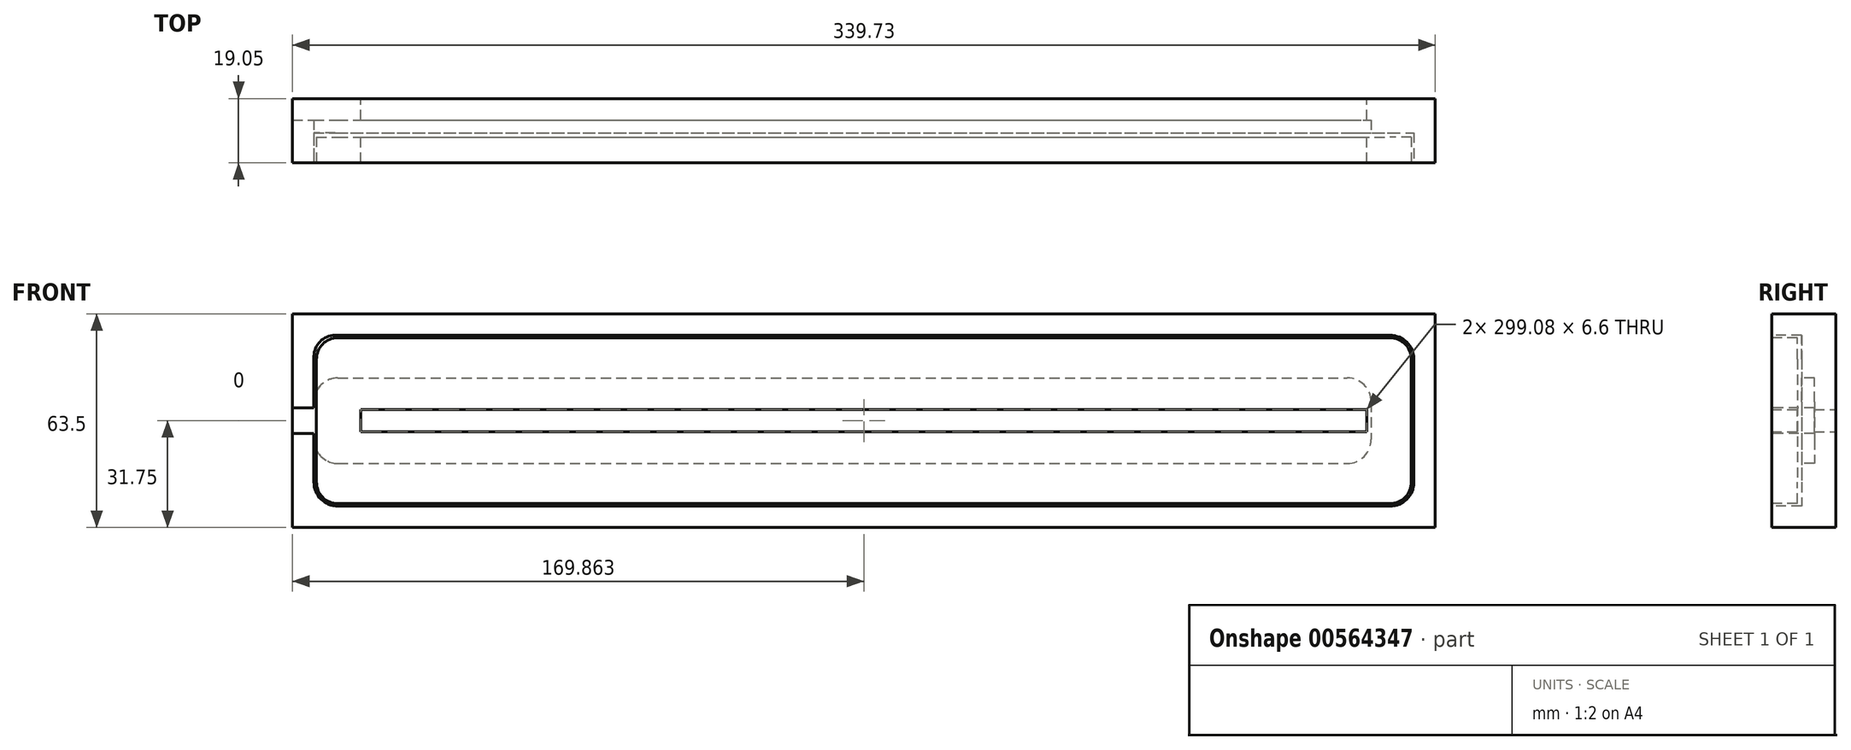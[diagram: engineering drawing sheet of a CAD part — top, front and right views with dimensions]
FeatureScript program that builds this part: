
annotation { "Feature Type Name" : "Feature", "Feature Type Description" : "" }
export const myFeature = defineFeature(function(context is Context, id is Id, definition is map)
    precondition{}
    {
        {
            var Q0;
            Q0=qCreatedBy(makeId("Front.planeOp"),FACE);
            var sketch = newSketch(context, id + "F0", { "sketchPlane" : qUnion([Q0])});
            skLineSegment(sketch, "E0.bottom", {"start": v(0, 0) * mm, "end": v(339.72, 0) * mm});
            skLineSegment(sketch, "E0.top", {"start": v(0, 63.5) * mm, "end": v(339.73, 63.5) * mm});
            skLineSegment(sketch, "E0.left", {"start": v(0, 0) * mm, "end": v(0, 63.5) * mm});
            skLineSegment(sketch, "E0.right", {"start": v(339.73, 0) * mm, "end": v(339.73, 63.5) * mm});
            skSolve(sketch);
        }
        {
            var Q0;
            Q0=makeQuery(id+"F0.imprint","IMPRINT",FACE,{"disambiguationData":[TD([[makeQuery(id+"F0.imprint","IMPRINT",EDGE,{"derivedFrom":sQuery(id+"F0.wireOp",EDGE,"E0.bottom")}),1.0]])]});
            extrude(context, id + "F1", {"entities" : qUnion([Q0]), "depth" : 19.05 * mm, "offsetDistance" : 25.4 * mm});
        }
        {
            var Q0;
            Q0=makeQuery(id+"F1.opExtrude","CAP_FACE",FACE,{"disambiguationData":[OSD([sQuery(id+"F0.wireOp",EDGE,"E0.bottom"),sQuery(id+"F0.wireOp",EDGE,"E0.top"),sQuery(id+"F0.wireOp",EDGE,"E0.left"),sQuery(id+"F0.wireOp",EDGE,"E0.right")])],"isStart":false});
            var sketch = newSketch(context, id + "F2", { "sketchPlane" : qUnion([Q0])});
            skLineSegment(sketch, "E1.bottom", {"start": v(13.46, 44.45) * mm, "end": v(313.56, 44.45) * mm});
            skLineSegment(sketch, "E1.top", {"start": v(13.46, 19.05) * mm, "end": v(313.56, 19.05) * mm});
            skLineSegment(sketch, "E1.left", {"start": v(6.35, 37.34) * mm, "end": v(6.35, 35.56) * mm});
            skLineSegment(sketch, "E1.right", {"start": v(320.68, 37.34) * mm, "end": v(320.68, 26.16) * mm});
            skLineSegment(sketch, "E2", {"start": v(6.35, 27.94) * mm, "end": v(0, 27.94) * mm});
            skLineSegment(sketch, "E3", {"start": v(0, 27.94) * mm, "end": v(0, 35.56) * mm});
            skLineSegment(sketch, "E4", {"start": v(0, 35.56) * mm, "end": v(6.35, 35.56) * mm});
            skLineSegment(sketch, "E5.trimOffspring", {"start": v(6.35, 27.94) * mm, "end": v(6.35, 26.16) * mm});
            skPoint(sketch, "E6.visualSharp", {"position": v(6.35, 44.45) * mm});
            skArc(sketch, "E6.filletArc", {"start": v(13.46, 44.45) * mm, "mid": v(8.43, 42.37) * mm, "end": v(6.35, 37.34) * mm});
            skPoint(sketch, "E7.visualSharp", {"position": v(6.35, 19.05) * mm});
            skArc(sketch, "E7.filletArc", {"start": v(6.35, 26.16) * mm, "mid": v(8.43, 21.13) * mm, "end": v(13.46, 19.05) * mm});
            skPoint(sketch, "E8.visualSharp", {"position": v(320.68, 44.45) * mm});
            skArc(sketch, "E8.filletArc", {"start": v(320.68, 37.34) * mm, "mid": v(318.6, 42.37) * mm, "end": v(313.56, 44.45) * mm});
            skPoint(sketch, "E9.visualSharp", {"position": v(320.68, 19.05) * mm});
            skArc(sketch, "E9.filletArc", {"start": v(313.56, 19.05) * mm, "mid": v(318.6, 21.13) * mm, "end": v(320.68, 26.16) * mm});
            skSolve(sketch);
        }
        {
            var Q0;
            Q0=makeQuery(id+"F2.imprint","IMPRINT",FACE,{"disambiguationData":[TD([[makeQuery(id+"F2.imprint","IMPRINT",EDGE,{"derivedFrom":sQuery(id+"F2.wireOp",EDGE,"E1.bottom")}),-1.0]])]});
            extrude(context, id + "F3", {"entities" : qUnion([Q0]), "operationType" : NewBodyOperationType.REMOVE, "oppositeDirection" : true, "depth" : 12.7 * mm, "offsetDistance" : 25.4 * mm});
        }
        {
            var Q0;
            Q0=makeQuery(id+"F1.opExtrude","CAP_FACE",FACE,{"disambiguationData":[OSD([sQuery(id+"F0.wireOp",EDGE,"E0.bottom"),sQuery(id+"F0.wireOp",EDGE,"E0.top"),sQuery(id+"F0.wireOp",EDGE,"E0.left"),sQuery(id+"F0.wireOp",EDGE,"E0.right")])],"isStart":false});
            var sketch = newSketch(context, id + "F4", { "sketchPlane" : qUnion([Q0])});
            skLineSegment(sketch, "E10.bottom", {"start": v(12.7, 57.15) * mm, "end": v(326.26, 57.15) * mm});
            skLineSegment(sketch, "E10.top", {"start": v(13.46, 6.35) * mm, "end": v(326.26, 6.35) * mm});
            skLineSegment(sketch, "E10.left", {"start": v(6.35, 50.8) * mm, "end": v(6.35, 13.46) * mm});
            skLineSegment(sketch, "E10.right", {"start": v(333.38, 50.04) * mm, "end": v(333.38, 13.46) * mm});
            skPoint(sketch, "E11.visualSharp", {"position": v(6.35, 57.15) * mm});
            skArc(sketch, "E11.filletArc", {"start": v(12.7, 57.15) * mm, "mid": v(8.2, 55.3) * mm, "end": v(6.35, 50.8) * mm});
            skPoint(sketch, "E12.visualSharp", {"position": v(6.35, 6.35) * mm});
            skArc(sketch, "E12.filletArc", {"start": v(6.35, 13.46) * mm, "mid": v(8.43, 8.43) * mm, "end": v(13.46, 6.35) * mm});
            skPoint(sketch, "E13.visualSharp", {"position": v(333.38, 6.35) * mm});
            skArc(sketch, "E13.filletArc", {"start": v(326.26, 6.35) * mm, "mid": v(331.3, 8.43) * mm, "end": v(333.38, 13.46) * mm});
            skPoint(sketch, "E14.visualSharp", {"position": v(333.38, 57.15) * mm});
            skArc(sketch, "E14.filletArc", {"start": v(333.38, 50.04) * mm, "mid": v(331.3, 55.07) * mm, "end": v(326.26, 57.15) * mm});
            skSolve(sketch);
        }
        {
            var Q0;
            {var subQ2=sQuery(id+"F4.wireOp",EDGE,"E10.bottom");Q0=makeQuery(id+"F4.imprint","IMPRINT",FACE,{"disambiguationData":[TD([[makeQuery(id+"F4.imprint","IMPRINT",EDGE,{"derivedFrom":subQ2}),-1.0]])]});}
            extrude(context, id + "F5", {"entities" : qUnion([Q0]), "operationType" : NewBodyOperationType.REMOVE, "oppositeDirection" : true, "depth" : 8.9 * mm, "offsetDistance" : 25.4 * mm});
        }
        {
            var Q0;
            Q0=makeQuery(id+"F1.opExtrude","CAP_FACE",FACE,{"disambiguationData":[OSD([sQuery(id+"F0.wireOp",EDGE,"E0.bottom"),sQuery(id+"F0.wireOp",EDGE,"E0.top"),sQuery(id+"F0.wireOp",EDGE,"E0.left"),sQuery(id+"F0.wireOp",EDGE,"E0.right")])],"isStart":false});
            var sketch = newSketch(context, id + "F6", { "sketchPlane" : qUnion([Q0])});
            skLineSegment(sketch, "E15.bottom", {"start": v(13.46, 56.39) * mm, "end": v(326.26, 56.39) * mm});
            skLineSegment(sketch, "E15.top", {"start": v(13.46, 7.11) * mm, "end": v(326.26, 7.11) * mm});
            skLineSegment(sketch, "E15.left", {"start": v(7.11, 50.04) * mm, "end": v(7.11, 13.46) * mm});
            skLineSegment(sketch, "E15.right", {"start": v(332.61, 50.04) * mm, "end": v(332.61, 13.46) * mm});
            skPoint(sketch, "E16.visualSharp", {"position": v(7.11, 7.11) * mm});
            skArc(sketch, "E16.filletArc", {"start": v(7.11, 13.46) * mm, "mid": v(8.97, 8.97) * mm, "end": v(13.46, 7.11) * mm});
            skPoint(sketch, "E17.visualSharp", {"position": v(7.11, 56.39) * mm});
            skArc(sketch, "E17.filletArc", {"start": v(13.46, 56.39) * mm, "mid": v(8.97, 54.53) * mm, "end": v(7.11, 50.04) * mm});
            skPoint(sketch, "E18.visualSharp", {"position": v(332.61, 56.39) * mm});
            skArc(sketch, "E18.filletArc", {"start": v(332.61, 50.04) * mm, "mid": v(330.75, 54.53) * mm, "end": v(326.26, 56.39) * mm});
            skPoint(sketch, "E19.visualSharp", {"position": v(332.61, 7.11) * mm});
            skArc(sketch, "E19.filletArc", {"start": v(326.26, 7.11) * mm, "mid": v(330.75, 8.97) * mm, "end": v(332.61, 13.46) * mm});
            skSolve(sketch);
        }
        {
            var Q0;
            Q0=makeQuery(id+"F6.imprint","IMPRINT",FACE,{"disambiguationData":[TD([[makeQuery(id+"F6.imprint","IMPRINT",EDGE,{"derivedFrom":sQuery(id+"F6.wireOp",EDGE,"E15.bottom")}),-1.0]])]});
            extrude(context, id + "F7", {"entities" : qUnion([Q0]), "depth" : -7.62 * mm, "offsetDistance" : 25.4 * mm});
        }
        {
            var Q0;
            Q0=makeQuery(id+"F1.opExtrude","CAP_FACE",FACE,{"disambiguationData":[OSD([sQuery(id+"F0.wireOp",EDGE,"E0.bottom"),sQuery(id+"F0.wireOp",EDGE,"E0.top"),sQuery(id+"F0.wireOp",EDGE,"E0.left"),sQuery(id+"F0.wireOp",EDGE,"E0.right")])],"isStart":true});
            var sketch = newSketch(context, id + "F8", { "sketchPlane" : qUnion([Q0])});
            skLineSegment(sketch, "E20.bottom", {"start": v(-319.4, 35.05) * mm, "end": v(-20.32, 35.05) * mm});
            skLineSegment(sketch, "E20.top", {"start": v(-319.4, 28.45) * mm, "end": v(-20.32, 28.45) * mm});
            skLineSegment(sketch, "E20.left", {"start": v(-319.4, 35.05) * mm, "end": v(-319.4, 28.45) * mm});
            skLineSegment(sketch, "E20.right", {"start": v(-20.32, 35.05) * mm, "end": v(-20.32, 28.45) * mm});
            skSolve(sketch);
        }
        {
            var Q0;
            Q0=makeQuery(id+"F8.imprint","IMPRINT",FACE,{"disambiguationData":[TD([[makeQuery(id+"F8.imprint","IMPRINT",EDGE,{"derivedFrom":sQuery(id+"F8.wireOp",EDGE,"E20.bottom")}),-1.0]])]});
            extrude(context, id + "F9", {"entities" : qUnion([Q0]), "operationType" : NewBodyOperationType.REMOVE, "oppositeDirection" : true, "depth" : 25.4 * mm, "offsetDistance" : 25.4 * mm});
        }
    });
